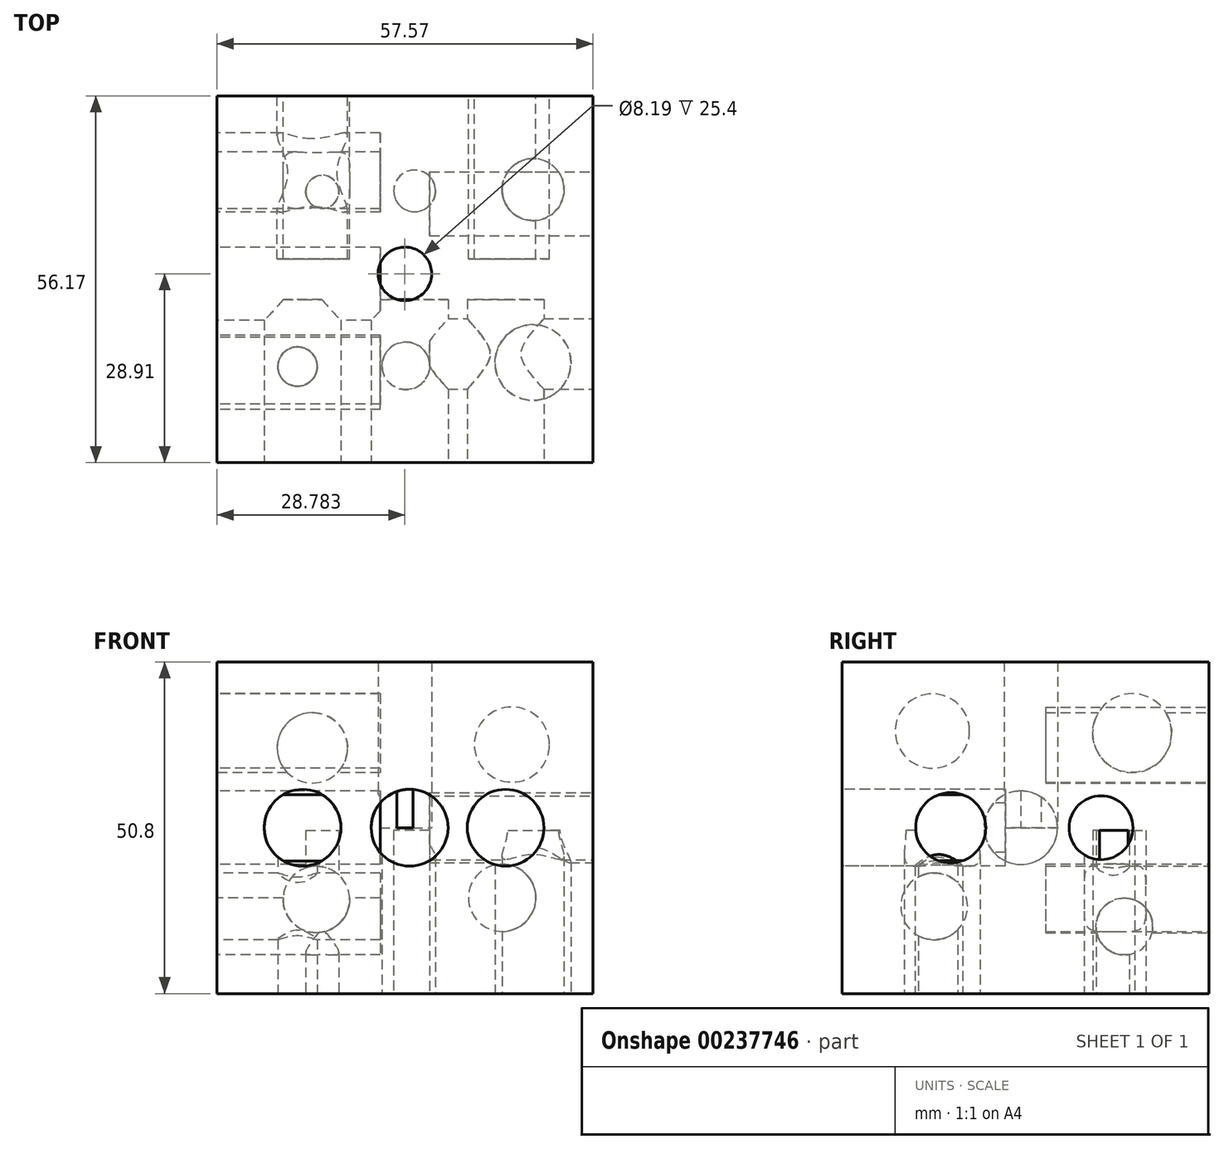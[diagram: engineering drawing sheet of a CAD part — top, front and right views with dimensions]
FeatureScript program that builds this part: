
annotation { "Feature Type Name" : "Feature", "Feature Type Description" : "" }
export const myFeature = defineFeature(function(context is Context, id is Id, definition is map)
    precondition{}
    {
        {
            var Q0;
            Q0=qCreatedBy(makeId("Top.planeOp"),FACE);
            var sketch = newSketch(context, id + "F0", { "sketchPlane" : qUnion([Q0])});
            skLineSegment(sketch, "E0.bottom", {"start": v(0, 0) * mm, "end": v(57.57, 0) * mm});
            skLineSegment(sketch, "E0.top", {"start": v(0, 56.17) * mm, "end": v(57.57, 56.17) * mm});
            skLineSegment(sketch, "E0.left", {"start": v(0, 0) * mm, "end": v(0, 56.17) * mm});
            skLineSegment(sketch, "E0.right", {"start": v(57.57, 0) * mm, "end": v(57.57, 56.17) * mm});
            skSolve(sketch);
        }
        {
            var Q0;
            Q0=makeQuery(id+"F0.imprint","IMPRINT",FACE,{"disambiguationData":[TD([[makeQuery(id+"F0.imprint","IMPRINT",EDGE,{"derivedFrom":sQuery(id+"F0.wireOp",EDGE,"E0.bottom")}),1.0]])]});
            extrude(context, id + "F1", {"entities" : qUnion([Q0]), "depth" : 25.4 * mm});
        }
        {
            var Q0;
            Q0=makeQuery(id+"F1.opExtrude","CAP_FACE",FACE,{"disambiguationData":[OSD([sQuery(id+"F0.wireOp",EDGE,"E0.bottom"),sQuery(id+"F0.wireOp",EDGE,"E0.top"),sQuery(id+"F0.wireOp",EDGE,"E0.left"),sQuery(id+"F0.wireOp",EDGE,"E0.right")])],"isStart":true});
            extrude(context, id + "F2", {"entities" : qUnion([Q0]), "operationType" : NewBodyOperationType.ADD, "depth" : 25.4 * mm});
        }
        {
            var Q0;
            Q0=qCreatedBy(makeId("Top.planeOp"),FACE);
            var sketch = newSketch(context, id + "F3", { "sketchPlane" : qUnion([Q0])});
            skCircle(sketch, "E1", {"center": v(28.78, 28.91) * mm, "radius": 4.1 * mm});
            skSolve(sketch);
        }
        {
            var Q0;
            Q0 = qSketchRegion(id + "F3", true);
            extrude(context, id + "F4", {"entities" : qUnion([Q0]), "operationType" : NewBodyOperationType.REMOVE, "depth" : 44.9 * mm});
        }
        {
            var Q0;
            {var subQ0=sQuery(id+"F0.wireOp",EDGE,"E0.right");Q0=makeQuery(id+"F2.boolean.opBoolean","MERGE",FACE,{"derivedFrom":[makeQuery(id+"F1.opExtrude","SWEPT_FACE",FACE,{"disambiguationData":[OSD([subQ0])]}),makeQuery(id+"F2.opExtrude","SWEPT_FACE",FACE,{"disambiguationData":[OSD([subQ0])]})]});}
            var sketch = newSketch(context, id + "F5", { "sketchPlane" : qUnion([Q0])});
            skCircle(sketch, "E2", {"center": v(16.65, 0) * mm, "radius": 5.37 * mm});
            skCircle(sketch, "E3", {"center": v(39.66, 0) * mm, "radius": 4.89 * mm});
            skSolve(sketch);
        }
        {
            var Q0;
            Q0 = qSketchRegion(id + "F5", true);
            extrude(context, id + "F6", {"entities" : qUnion([Q0]), "operationType" : NewBodyOperationType.REMOVE, "oppositeDirection" : true, "depth" : 25 * mm});
        }
        {
            var Q0;
            {var subQ0=sQuery(id+"F0.wireOp",EDGE,"E0.bottom");Q0=makeQuery(id+"F2.boolean.opBoolean","MERGE",FACE,{"derivedFrom":[makeQuery(id+"F1.opExtrude","SWEPT_FACE",FACE,{"disambiguationData":[OSD([subQ0])]}),makeQuery(id+"F2.opExtrude","SWEPT_FACE",FACE,{"disambiguationData":[OSD([subQ0])]})]});}
            var sketch = newSketch(context, id + "F7", { "sketchPlane" : qUnion([Q0])});
            skCircle(sketch, "E4", {"center": v(13.1, 0) * mm, "radius": 5.87 * mm});
            skCircle(sketch, "E5", {"center": v(44.2, 0) * mm, "radius": 5.87 * mm});
            skCircle(sketch, "E6", {"center": v(29.5, 0) * mm, "radius": 5.89 * mm});
            skSolve(sketch);
        }
        {
            var Q0;
            Q0 = qSketchRegion(id + "F7", true);
            extrude(context, id + "F8", {"entities" : qUnion([Q0]), "operationType" : NewBodyOperationType.REMOVE, "oppositeDirection" : true, "depth" : 25 * mm});
        }
        {
            var Q0;
            {var subQ0=sQuery(id+"F0.wireOp",EDGE,"E0.top");Q0=makeQuery(id+"F2.boolean.opBoolean","MERGE",FACE,{"derivedFrom":[makeQuery(id+"F1.opExtrude","SWEPT_FACE",FACE,{"disambiguationData":[OSD([subQ0])]}),makeQuery(id+"F2.opExtrude","SWEPT_FACE",FACE,{"disambiguationData":[OSD([subQ0])]})]});}
            var sketch = newSketch(context, id + "F9", { "sketchPlane" : qUnion([Q0])});
            skCircle(sketch, "E7", {"center": v(-45.18, 12.73) * mm, "radius": 5.75 * mm});
            skCircle(sketch, "E8", {"center": v(-14.6, 12.23) * mm, "radius": 5.39 * mm});
            skCircle(sketch, "E9", {"center": v(-43.68, -10.73) * mm, "radius": 5.15 * mm});
            skCircle(sketch, "E10", {"center": v(-15.23, -10.98) * mm, "radius": 5.1 * mm});
            skSolve(sketch);
        }
        {
            var Q0;
            Q0 = qSketchRegion(id + "F9", true);
            extrude(context, id + "F10", {"entities" : qUnion([Q0]), "operationType" : NewBodyOperationType.REMOVE, "oppositeDirection" : true, "depth" : 25 * mm});
        }
        {
            var Q0;
            {var subQ0=sQuery(id+"F0.wireOp",EDGE,"E0.left");Q0=makeQuery(id+"F2.boolean.opBoolean","MERGE",FACE,{"derivedFrom":[makeQuery(id+"F1.opExtrude","SWEPT_FACE",FACE,{"disambiguationData":[OSD([subQ0])]}),makeQuery(id+"F2.opExtrude","SWEPT_FACE",FACE,{"disambiguationData":[OSD([subQ0])]})]});}
            var sketch = newSketch(context, id + "F11", { "sketchPlane" : qUnion([Q0])});
            skCircle(sketch, "E11", {"center": v(-27.4, 0) * mm, "radius": 5.61 * mm});
            skCircle(sketch, "E12", {"center": v(-13.83, 14.8) * mm, "radius": 5.69 * mm});
            skCircle(sketch, "E13", {"center": v(-44.43, 14.48) * mm, "radius": 6.05 * mm});
            skCircle(sketch, "E14", {"center": v(-43.24, -15.13) * mm, "radius": 4.35 * mm});
            skCircle(sketch, "E15", {"center": v(-14.1, -12.05) * mm, "radius": 5.11 * mm});
            skSolve(sketch);
        }
        {
            var Q0;
            Q0 = qSketchRegion(id + "F11", true);
            extrude(context, id + "F12", {"entities" : qUnion([Q0]), "operationType" : NewBodyOperationType.REMOVE, "oppositeDirection" : true, "depth" : 25 * mm});
        }
        {
            var Q0;
            Q0=makeQuery(id+"F2.opExtrude","CAP_FACE",FACE,{"disambiguationData":[OSD([sQuery(id+"F0.wireOp",EDGE,"E0.bottom"),sQuery(id+"F0.wireOp",EDGE,"E0.top"),sQuery(id+"F0.wireOp",EDGE,"E0.left"),sQuery(id+"F0.wireOp",EDGE,"E0.right")])],"isStart":false});
            var sketch = newSketch(context, id + "F13", { "sketchPlane" : qUnion([Q0])});
            skCircle(sketch, "E16", {"center": v(16.14, -41.48) * mm, "radius": 2.54 * mm});
            skCircle(sketch, "E17", {"center": v(30.26, -41.62) * mm, "radius": 3.19 * mm});
            skCircle(sketch, "E18", {"center": v(48.42, -41.8) * mm, "radius": 4.74 * mm});
            skCircle(sketch, "E19", {"center": v(12.34, -14.71) * mm, "radius": 3.02 * mm});
            skCircle(sketch, "E20", {"center": v(28.93, -14.83) * mm, "radius": 3.65 * mm});
            skCircle(sketch, "E21", {"center": v(48.4, -15.33) * mm, "radius": 5.8 * mm});
            skSolve(sketch);
        }
        {
            var Q0;
            Q0 = qSketchRegion(id + "F13", true);
            extrude(context, id + "F14", {"entities" : qUnion([Q0]), "operationType" : NewBodyOperationType.REMOVE, "oppositeDirection" : true, "depth" : 25 * mm});
        }
    });
